# Revit family: AISC Pipe Shapes-Top
name_source: partatom
category: Detail Items
revit_build: Autodesk Revit Architecture 2012 (Build: 20110210_1515)
units: mm (PartAtom-declared; Revit-internal decimal feet)

## types (37) — shared parameters
Keynote = 05 12 00.K0

## per-type parameters (varying)
| type | A | Gauge | ID | OD | W | t |
| Pipe1/2STD | 0 SF | Standard | 0' - 0 5/8" | 0' - 0 27/32" | 0.85 | 0' - 0 3/32" |
| Pipe3/4STD | 0 SF | Standard | 0' - 0 13/16" | 0' - 1 1/16" | 1.13 | 0' - 0 1/8" |
| Pipe1STD | 0 SF | Standard | 0' - 1 1/16" | 0' - 1 5/16" | 1.68 | 0' - 0 1/8" |
| Pipe1-1/4STD | 0 SF | Standard | 0' - 1 3/8" | 0' - 1 21/32" | 2.27 | 0' - 0 1/8" |
| Pipe1-1/2STD | 0.01 SF | Standard | 0' - 1 5/8" | 0' - 1 29/32" | 2.72 | 0' - 0 5/32" |
| Pipe2STD | 0.01 SF | Standard | 0' - 2 1/16" | 0' - 2 3/8" | 3.66 | 0' - 0 5/32" |
| Pipe2-1/2STD | 0.01 SF | Standard | 0' - 2 15/32" | 0' - 2 7/8" | 5.8 | 0' - 0 3/16" |
| Pipe3STD | 0.01 SF | Standard | 0' - 3 1/16" | 0' - 3 1/2" | 7.58 | 0' - 0 7/32" |
| Pipe3-1/2STD | 0.02 SF | Standard | 0' - 3 9/16" | 0' - 4" | 9.12 | 0' - 0 7/32" |
| Pipe4STD | 0.02 SF | Standard | 0' - 4 1/32" | 0' - 4 1/2" | 10.8 | 0' - 0 1/4" |
| Pipe5STD | 0.03 SF | Standard | 0' - 5 1/16" | 0' - 5 9/16" | 14.6 | 0' - 0 1/4" |
| Pipe6STD | 0.04 SF | Standard | 0' - 6 1/16" | 0' - 6 5/8" | 19 | 0' - 0 9/32" |
| Pipe8STD | 0.05 SF | Standard | 0' - 7 31/32" | 0' - 8 5/8" | 28.6 | 0' - 0 5/16" |
| Pipe10STD | 0.08 SF | Standard | 0' - 10" | 0' - 10 3/4" | 40.5 | 0' - 0 3/8" |
| Pipe12STD | 0.09 SF | Standard | 1' - 0" | 1' - 0 3/4" | 49.6 | 0' - 0 3/8" |
| Pipe1/2XS | 0 SF | X Strong | 0' - 0 17/32" | 0' - 0 27/32" | 1.09 | 0' - 0 5/32" |
| Pipe3/4XS | 0 SF | X Strong | 0' - 0 3/4" | 0' - 1 1/16" | 1.48 | 0' - 0 5/32" |
| Pipe1XS | 0 SF | X Strong | 0' - 0 31/32" | 0' - 1 5/16" | 2.17 | 0' - 0 3/16" |
| Pipe1-1/4XS | 0.01 SF | X Strong | 0' - 1 9/32" | 0' - 1 21/32" | 3 | 0' - 0 3/16" |
| Pipe1-1/2XS | 0.01 SF | X Strong | 0' - 1 1/2" | 0' - 1 29/32" | 3.63 | 0' - 0 3/16" |
| Pipe2XS | 0.01 SF | X Strong | 0' - 1 15/16" | 0' - 2 3/8" | 5.03 | 0' - 0 7/32" |
| Pipe2-1/2XS | 0.01 SF | X Strong | 0' - 2 5/16" | 0' - 2 7/8" | 7.67 | 0' - 0 9/32" |
| Pipe3XS | 0.02 SF | X Strong | 0' - 2 29/32" | 0' - 3 1/2" | 10.3 | 0' - 0 5/16" |
| Pipe3-1/2XS | 0.02 SF | X Strong | 0' - 3 3/8" | 0' - 4" | 12.5 | 0' - 0 5/16" |
| Pipe4XS | 0.03 SF | X Strong | 0' - 3 13/16" | 0' - 4 1/2" | 15 | 0' - 0 11/32" |
| Pipe5XS | 0.04 SF | X Strong | 0' - 4 13/16" | 0' - 5 9/16" | 20.8 | 0' - 0 3/8" |
| Pipe6XS | 0.05 SF | X Strong | 0' - 5 3/4" | 0' - 6 5/8" | 28.6 | 0' - 0 7/16" |
| Pipe8XS | 0.08 SF | X Strong | 0' - 7 5/8" | 0' - 8 5/8" | 43.4 | 0' - 0 1/2" |
| Pipe10XS | 0.1 SF | X Strong | 0' - 9 3/4" | 0' - 10 3/4" | 54.8 | 0' - 0 1/2" |
| Pipe12XS | 0.12 SF | X Strong | 0' - 11 3/4" | 1' - 0 3/4" | 65.5 | 0' - 0 1/2" |
| Pipe2XXS | 0.02 SF | XX Strong | 0' - 1 1/2" | 0' - 2 3/8" | 9.04 | 0' - 0 7/16" |
| Pipe2-1/2XXS | 0.03 SF | XX Strong | 0' - 1 25/32" | 0' - 2 7/8" | 13.7 | 0' - 0 9/16" |
| Pipe3XXS | 0.04 SF | XX Strong | 0' - 2 5/16" | 0' - 3 1/2" | 18.6 | 0' - 0 19/32" |
| Pipe4XXS | 0.05 SF | XX Strong | 0' - 3 5/32" | 0' - 4 1/2" | 27.6 | 0' - 0 11/16" |
| Pipe5XXS | 0.07 SF | XX Strong | 0' - 4 1/16" | 0' - 5 9/16" | 38.6 | 0' - 0 3/4" |
| Pipe6XXS | 0.1 SF | XX Strong | 0' - 4 29/32" | 0' - 6 5/8" | 53.2 | 0' - 0 7/8" |
| Pipe8XXS | 0.14 SF | XX Strong | 0' - 6 7/8" | 0' - 8 5/8" | 72.5 | 0' - 0 7/8" |

## geometry (parser evidence)
native form markers: Sweep x1
no freeform markers — native parametric forms only
